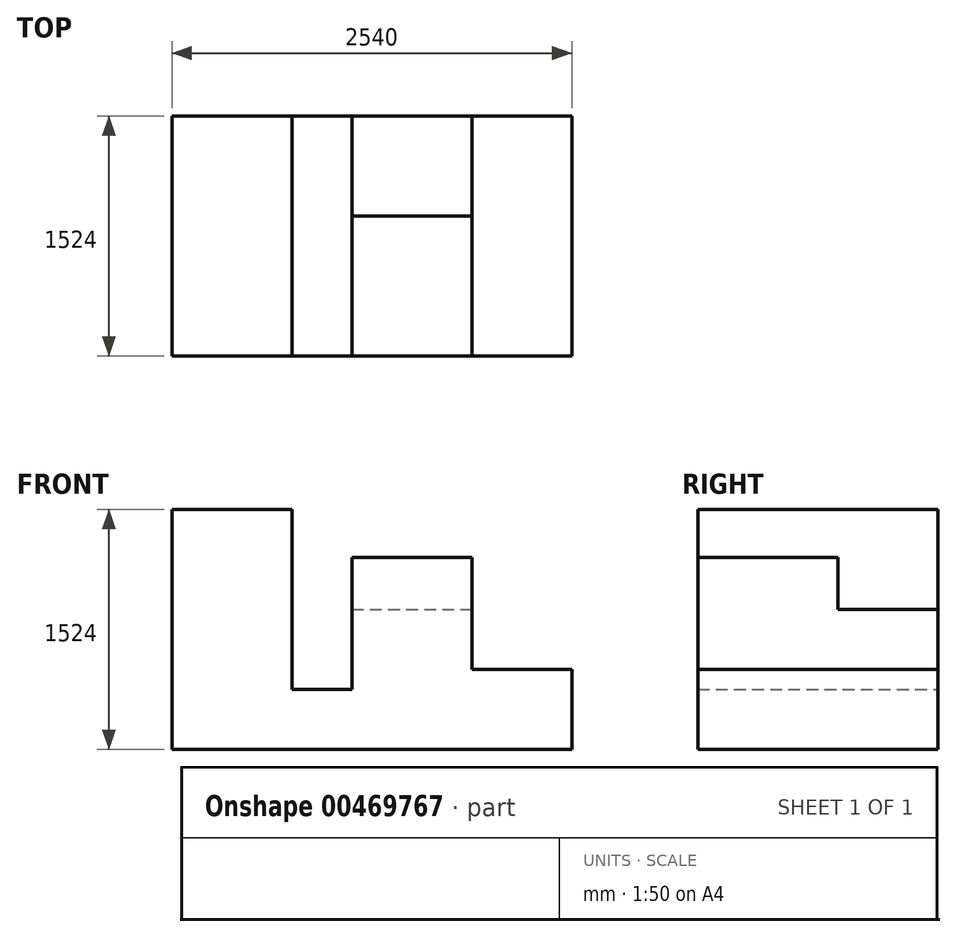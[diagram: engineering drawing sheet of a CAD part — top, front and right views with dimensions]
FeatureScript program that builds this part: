
annotation { "Feature Type Name" : "Feature", "Feature Type Description" : "" }
export const myFeature = defineFeature(function(context is Context, id is Id, definition is map)
    precondition{}
    {
        {
            var Q0;
            Q0=qCreatedBy(makeId("Front.planeOp"),FACE);
            var sketch = newSketch(context, id + "F0", { "sketchPlane" : qUnion([Q0])});
            skLineSegment(sketch, "E0.bottom", {"start": v(-1270, -762) * mm, "end": v(1270, -762) * mm});
            skLineSegment(sketch, "E0.top", {"start": v(-1270, 762) * mm, "end": v(-508, 762) * mm});
            skLineSegment(sketch, "E0.left", {"start": v(-1270, -762) * mm, "end": v(-1270, 762) * mm});
            skLineSegment(sketch, "E0.right", {"start": v(1270, -762) * mm, "end": v(1270, -254) * mm});
            skPoint(sketch, "E0.middle", {"position": v(0, 0) * mm});
            skLineSegment(sketch, "E1.top", {"start": v(-508, -381) * mm, "end": v(-127, -381) * mm});
            skLineSegment(sketch, "E1.left", {"start": v(-508, 762) * mm, "end": v(-508, -381) * mm});
            skLineSegment(sketch, "E1.right", {"start": v(-127, 457.2) * mm, "end": v(-127, -381) * mm});
            skLineSegment(sketch, "E2", {"start": v(-127, 457.2) * mm, "end": v(635, 457.2) * mm});
            skLineSegment(sketch, "E3", {"start": v(635, 457.2) * mm, "end": v(635, -254) * mm});
            skLineSegment(sketch, "E4", {"start": v(635, -254) * mm, "end": v(1270, -254) * mm});
            skPoint(sketch, "E5.orphan", {"position": v(1270, 762) * mm});
            skSolve(sketch);
        }
        {
            var Q0;
            Q0 = qSketchRegion(id + "F0", true);
            extrude(context, id + "F1", {"entities" : qUnion([Q0]), "endBound" : BoundingType.SYMMETRIC, "depth" : 1524 * mm});
        }
        {
            var Q0;
            Q0=makeQuery(id+"F1.opExtrude","SWEPT_FACE",FACE,{"disambiguationData":[OSD([sQuery(id+"F0.wireOp",EDGE,"E3")])]});
            var sketch = newSketch(context, id + "F2", { "sketchPlane" : qUnion([Q0])});
            skLineSegment(sketch, "E6.bottom", {"start": v(762, 457.2) * mm, "end": v(127, 457.2) * mm});
            skLineSegment(sketch, "E6.top", {"start": v(762, 127) * mm, "end": v(127, 127) * mm});
            skLineSegment(sketch, "E6.left", {"start": v(762, 457.2) * mm, "end": v(762, 127) * mm});
            skLineSegment(sketch, "E6.right", {"start": v(127, 457.2) * mm, "end": v(127, 127) * mm});
            skSolve(sketch);
        }
        {
            var Q0;
            Q0 = qSketchRegion(id + "F2", true);
            extrude(context, id + "F3", {"entities" : qUnion([Q0]), "operationType" : NewBodyOperationType.REMOVE, "oppositeDirection" : true, "depth" : 762 * mm});
        }
    });
